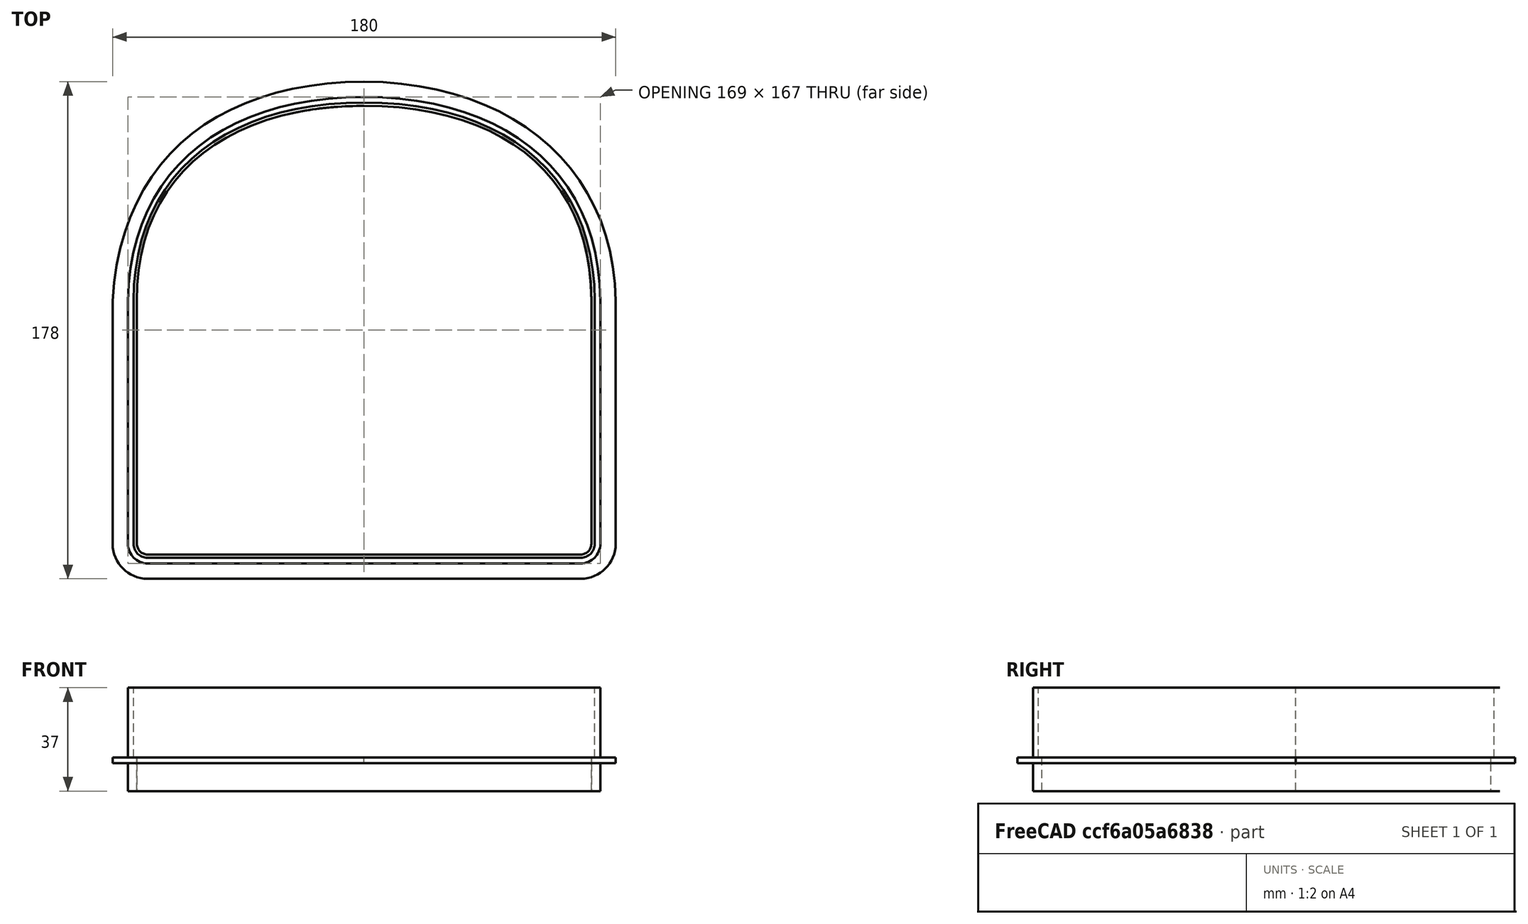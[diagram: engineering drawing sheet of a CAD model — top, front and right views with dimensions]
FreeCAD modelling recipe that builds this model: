
FCSTD DOCUMENT  (FreeCAD 0.20R29410 (Git))
Label: CatDoorTunnel
License: All rights reserved
LicenseURL: http://en.wikipedia.org/wiki/All_rights_reserved
objects: Sketcher::SketchObject×6, PartDesign::Pad×5, PartDesign::Chamfer×2, PartDesign::Body×1
note: 21 computed .brp shape members not serialized (recipe doc carries the construction recipe); baked Part::Feature solids carry a one-line shape summary decoded from their .brp

FEATURE [Sketcher::SketchObject] Sketch
  FullyConstrained = true
  MapMode = 5
  Support = -> [XY_Plane]
  sketch-geometry (78):
    g0: LineSegment StartX=-82.5 StartY=-87 StartZ=0 EndX=-82.5 EndY=-2.2737e-12 EndZ=0
    g1: LineSegment StartX=82.5 StartY=-1.3709e-12 StartZ=0 EndX=82.5 EndY=-87 EndZ=0
    g2: LineSegment StartX=77.5 StartY=-92 StartZ=0 EndX=-77.5 EndY=-92 EndZ=0
    g3: ArcOfCircle CenterX=-77.5 CenterY=-87 CenterZ=0 NormalX=0 NormalY=0 NormalZ=1 AngleXU=0 Radius=5 StartAngle=3.14159 EndAngle=4.71239
    g4: ArcOfCircle CenterX=77.5 CenterY=-87 CenterZ=0 NormalX=0 NormalY=0 NormalZ=1 AngleXU=0 Radius=5 StartAngle=4.71239 EndAngle=6.28319
    g5: LineSegment StartX=-82.5 StartY=45 StartZ=0 EndX=-50 EndY=45 EndZ=0
    g6: LineSegment StartX=-50 StartY=45 StartZ=0 EndX=50 EndY=45 EndZ=0
    g7: LineSegment StartX=50 StartY=45 StartZ=0 EndX=82.5 EndY=45 EndZ=0
    g8: LineSegment StartX=-50 StartY=71 StartZ=0 EndX=-50 EndY=45 EndZ=0
    g9: LineSegment StartX=50 StartY=71 StartZ=0 EndX=50 EndY=45 EndZ=0
    g10: LineSegment StartX=-82.5 StartY=71 StartZ=0 EndX=-50 EndY=71 EndZ=0
    g11: LineSegment StartX=50 StartY=71 StartZ=0 EndX=82.5 EndY=71 EndZ=0
    g12: LineSegment StartX=-82.5 StartY=45 StartZ=0 EndX=-82.5 EndY=71 EndZ=0
    g13: LineSegment StartX=82.5 StartY=71 StartZ=0 EndX=82.5 EndY=45 EndZ=0
    g14: LineSegment StartX=-50 StartY=71 StartZ=0 EndX=-8.37969 EndY=71 EndZ=0
    g15: LineSegment StartX=-8.37969 StartY=71 StartZ=0 EndX=-5.347e-13 EndY=71 EndZ=0
    g16: LineSegment StartX=-5.344e-13 StartY=71 StartZ=0 EndX=8.37969 EndY=71 EndZ=0
    g17: LineSegment StartX=8.37969 StartY=71 StartZ=0 EndX=50 EndY=71 EndZ=0
    g18: LineSegment StartX=-82.5 StartY=-2.2737e-12 StartZ=0 EndX=-82.5 EndY=3.37969 EndZ=0
    g19: LineSegment StartX=-82.5 StartY=3.37969 StartZ=0 EndX=-82.5 EndY=45 EndZ=0
    g20: LineSegment StartX=82.5 StartY=45 StartZ=0 EndX=82.5 EndY=3.37969 EndZ=0
    g21: LineSegment StartX=82.5 StartY=3.37969 StartZ=0 EndX=82.5 EndY=-1.3709e-12 EndZ=0
    g22: LineSegment StartX=-82.5 StartY=3.37969 StartZ=0 EndX=82.5 EndY=3.37969 EndZ=0
    g23: LineSegment StartX=-8.37969 StartY=71 StartZ=0 EndX=-8.37969 EndY=-92 EndZ=0
    g24: LineSegment StartX=50 StartY=71 StartZ=0 EndX=82.5 EndY=45 EndZ=0
    g25: LineSegment StartX=-82.5 StartY=45 StartZ=0 EndX=-50 EndY=71 EndZ=0
    g26: LineSegment StartX=-5.344e-13 StartY=73 StartZ=0 EndX=-5.344e-13 EndY=71 EndZ=0
    g27: LineSegment StartX=-5.344e-13 StartY=71 StartZ=0 EndX=-5.344e-13 EndY=69.8 EndZ=0
    g28: LineSegment StartX=50.662 StartY=72.8873 StartZ=0 EndX=50 EndY=71 EndZ=0
    g29: LineSegment StartX=50 StartY=71 StartZ=0 EndX=49.6028 EndY=69.8676 EndZ=0
    g30: LineSegment StartX=49.6028 StartY=69.8676 StartZ=0 EndX=45.4398 EndY=58 EndZ=0
    g31: LineSegment StartX=84.3026 StartY=45.8664 StartZ=0 EndX=82.5 EndY=45 EndZ=0
    g32: LineSegment StartX=82.5 StartY=45 StartZ=0 EndX=81.4184 EndY=44.4802 EndZ=0
    g33: LineSegment StartX=81.4184 StartY=44.4802 StartZ=0 EndX=66.25 EndY=37.1898 EndZ=0
    g34: LineSegment StartX=-50.662 StartY=72.8873 StartZ=0 EndX=-50 EndY=71 EndZ=0
    g35: LineSegment StartX=-50 StartY=71 StartZ=0 EndX=-49.6028 EndY=69.8676 EndZ=0
    g36: LineSegment StartX=-49.6028 StartY=69.8676 StartZ=0 EndX=-45.4398 EndY=58 EndZ=0
    g37: LineSegment StartX=-83.7309 StartY=46.5763 StartZ=0 EndX=-82.5 EndY=45 EndZ=0
    g38: LineSegment StartX=-82.5 StartY=45 StartZ=0 EndX=-81.7615 EndY=44.0542 EndZ=0
    g39: LineSegment StartX=-81.7615 StartY=44.0542 StartZ=0 EndX=-66.25 EndY=24.1898 EndZ=0
    g40: LineSegment StartX=-82.5 StartY=-2.2737e-12 StartZ=0 EndX=-84.5 EndY=-2.2737e-12 EndZ=0
    g41: LineSegment StartX=-82.5 StartY=-2.2737e-12 StartZ=0 EndX=-81.3 EndY=-2.2737e-12 EndZ=0
    g42: LineSegment StartX=-82.5 StartY=-87 StartZ=0 EndX=-84.5 EndY=-87 EndZ=0
    g43: LineSegment StartX=-82.5 StartY=-87 StartZ=0 EndX=-81.3 EndY=-87 EndZ=0
    g44: LineSegment StartX=-77.5 StartY=-92 StartZ=0 EndX=-77.5 EndY=-94 EndZ=0
    g45: LineSegment StartX=-77.5 StartY=-92 StartZ=0 EndX=-77.5 EndY=-90.8 EndZ=0
    g46: LineSegment StartX=77.5 StartY=-92 StartZ=0 EndX=77.5 EndY=-94 EndZ=0
    g47: LineSegment StartX=77.5 StartY=-92 StartZ=0 EndX=77.5 EndY=-90.8 EndZ=0
    g48: LineSegment StartX=82.5 StartY=-87 StartZ=0 EndX=81.3 EndY=-87 EndZ=0
    g49: LineSegment StartX=82.5 StartY=-87 StartZ=0 EndX=84.5 EndY=-87 EndZ=0
    g50: LineSegment StartX=82.5 StartY=-1.3709e-12 StartZ=0 EndX=84.5 EndY=-1.3709e-12 EndZ=0
    g51: LineSegment StartX=82.5 StartY=-1.3709e-12 StartZ=0 EndX=81.3 EndY=-1.3709e-12 EndZ=0
    g52: ArcOfCircle CenterX=-77.5 CenterY=-87 CenterZ=0 NormalX=0 NormalY=0 NormalZ=1 AngleXU=0 Radius=7 StartAngle=3.14159 EndAngle=4.71239
    g53: ArcOfCircle CenterX=-77.5 CenterY=-87 CenterZ=0 NormalX=0 NormalY=0 NormalZ=1 AngleXU=0 Radius=3.8 StartAngle=3.14159 EndAngle=4.71239
    g54: ArcOfCircle CenterX=77.5 CenterY=-87 CenterZ=0 NormalX=0 NormalY=0 NormalZ=1 AngleXU=0 Radius=3.8 StartAngle=4.71239 EndAngle=6.28319
    g55: ArcOfCircle CenterX=77.5 CenterY=-87 CenterZ=0 NormalX=0 NormalY=0 NormalZ=1 AngleXU=0 Radius=7 StartAngle=4.71239 EndAngle=6.28319
    g56: LineSegment StartX=-77.5 StartY=-94 StartZ=0 EndX=77.5 EndY=-94 EndZ=0
    g57: LineSegment StartX=-77.5 StartY=-90.8 StartZ=0 EndX=77.5 EndY=-90.8 EndZ=0
    g58: LineSegment StartX=84.5 StartY=-87 StartZ=0 EndX=84.5 EndY=-1.3642e-12 EndZ=0
    g59: LineSegment StartX=81.3 StartY=-1.3709e-12 StartZ=0 EndX=81.3 EndY=-87 EndZ=0
    g60: LineSegment StartX=-81.3 StartY=-87 StartZ=0 EndX=-81.3 EndY=-2.2737e-12 EndZ=0
    g61: LineSegment StartX=-84.5 StartY=-87 StartZ=0 EndX=-84.5 EndY=-2.2737e-12 EndZ=0
    g62: LineSegment StartX=84.5 StartY=-1.3709e-12 StartZ=0 EndX=90 EndY=-1.3709e-12 EndZ=0
    g63: LineSegment StartX=84.5 StartY=-87 StartZ=0 EndX=90 EndY=-87 EndZ=0
    g64: LineSegment StartX=77.5 StartY=-94 StartZ=0 EndX=77.5 EndY=-99.5 EndZ=0
    g65: LineSegment StartX=-77.5 StartY=-94 StartZ=0 EndX=-77.5 EndY=-99.5 EndZ=0
    g66: LineSegment StartX=-84.5 StartY=-87 StartZ=0 EndX=-90 EndY=-87 EndZ=0
    g67: LineSegment StartX=-84.5 StartY=-2.2737e-12 StartZ=0 EndX=-90 EndY=-2.2737e-12 EndZ=0
    g68: LineSegment StartX=-83.7309 StartY=46.5763 StartZ=0 EndX=-87.1159 EndY=50.9113 EndZ=0
    g69: LineSegment StartX=-50.662 StartY=72.8873 StartZ=0 EndX=-52.4826 EndY=78.0772 EndZ=0
    g70: LineSegment StartX=-5.344e-13 StartY=73 StartZ=0 EndX=-5.344e-13 EndY=78.5 EndZ=0
    g71: LineSegment StartX=50.662 StartY=72.8873 StartZ=0 EndX=52.4826 EndY=78.0772 EndZ=0
    g72: LineSegment StartX=84.3026 StartY=45.8664 StartZ=0 EndX=89.2598 EndY=48.2489 EndZ=0
    g73: LineSegment StartX=-77.5 StartY=-99.5 StartZ=0 EndX=77.5 EndY=-99.5 EndZ=0
    g74: LineSegment StartX=-90 StartY=-2.2737e-12 StartZ=0 EndX=-90 EndY=-87 EndZ=0
    g75: LineSegment StartX=90 StartY=-87 StartZ=0 EndX=90 EndY=-1.3642e-12 EndZ=0
    g76: ArcOfCircle CenterX=-77.5 CenterY=-87 CenterZ=0 NormalX=0 NormalY=0 NormalZ=1 AngleXU=0 Radius=12.5 StartAngle=3.14159 EndAngle=4.71239
    g77: ArcOfCircle CenterX=77.5 CenterY=-87 CenterZ=0 NormalX=0 NormalY=0 NormalZ=1 AngleXU=0 Radius=12.5 StartAngle=4.71239 EndAngle=6.28319
  constraints (212):
    c: Coincident(g11,g13)
    c: Coincident(g12,g10)
    c: Coincident(g0,g18)
    c: Vertical(g0)
    c: Coincident(g21,g1)
    c: Horizontal(g2)
    c: Tangent(g0,g3) = 1.5708
    c: Tangent(g2,g3) = 1.5708
    c: Tangent(g1,g4) = 1.5708
    c: Vertical(g1)
    c: DistanceY(g2,g10) = 163
    c: DistanceY(g2,g0) = 92
    c: Radius(g3) = 5
    c: Horizontal(g5)
    c: Coincident(g6,g5)
    c: Horizontal(g6)
    c: Coincident(g7,g6)
    c: Horizontal(g7)
    c: Coincident(g8,g5)
    c: Vertical(g8)
    c: Vertical(g9)
    c: Coincident(g6,g9)
    c: Equal(g7,g5)
    c: DistanceY(g0,g5) = 45
    c: Coincident(g10,g14)
    c: Horizontal(g10)
    c: Coincident(g17,g11)
    c: Horizontal(g11)
    c: Coincident(g9,g17)
    c: Coincident(g8,g10)
    c: Coincident(g19,g12)
    c: Vertical(g12)
    c: Coincident(g13,g20)
    c: Vertical(g13)
    c: Coincident(g7,g13)
    c: Coincident(g5,g19)
    c: Coincident(g15,g16)
    c: Coincident(g14,g15)
    c: Horizontal(g14)
    c: Horizontal(g15)
    c: Coincident(g16,g17)
    c: Horizontal(g16)
    c: Equal(g15,g16)
    c: Equal(g14,g17)
    c: Tangent(g2,g4) = 1.5708
    c: Equal(g3,g4)
    c: Coincident(g18,g19)
    c: Vertical(g18)
    c: Vertical(g19)
    c: Coincident(g20,g21)
    c: Vertical(g20)
    c: Vertical(g21)
    c: Equal(g18,g21)
    c: Coincident(g22,g18)
    c: Coincident(g22,g20)
    c: Horizontal(g22)
    c: Coincident(g23,g14)
    c: PointOnObject(g23,g2)
    c: Vertical(g23)
    c: Coincident(g24,g9)
    c: Coincident(g24,g7)
    c: Coincident(g25,g5)
    c: Coincident(g25,g8)
    c: Equal(g17,g24)
    c: Equal(g24,g20)
    c: Equal(g19,g25)
    c: DistanceX(g8,g15) = 50
    c: Coincident(g26,g15)
    c: Vertical(g26)
    c: Coincident(g26,g27)
    c: Vertical(g27)
    c: Coincident(g28,g9)
    c: Coincident(g28,g29)
    c: Coincident(g29,g30)
    c: Parallel(g30,g29)
    c: Parallel(g29,g28)
    c: Symmetric(g7,g16,g30)
    c: Coincident(g31,g7)
    c: Coincident(g31,g32)
    c: Coincident(g32,g33)
    c: Parallel(g33,g32)
    c: Parallel(g32,g31)
    c: Symmetric(g28,g20,g33)
    c: Coincident(g34,g8)
    c: Coincident(g34,g35)
    c: Coincident(g35,g36)
    c: Coincident(g37,g5)
    c: Coincident(g37,g38)
    c: Coincident(g38,g39)
    c: Parallel(g36,g35)
    c: Parallel(g35,g34)
    c: Parallel(g37,g38)
    c: Parallel(g38,g39)
    c: Symmetric(g18,g5,g39)
    c: Symmetric(g37,g14,g36)
    c: Coincident(g40,g0)
    c: Horizontal(g40)
    c: Coincident(g41,g0)
    c: Horizontal(g41)
    c: Coincident(g42,g0)
    c: Coincident(g43,g0)
    c: Horizontal(g43)
    c: Coincident(g44,g2)
    c: Vertical(g44)
    c: Coincident(g45,g2)
    c: Vertical(g45)
    c: Coincident(g46,g2)
    c: Vertical(g46)
    c: Coincident(g47,g2)
    c: Vertical(g47)
    c: Coincident(g48,g1)
    c: Horizontal(g48)
    c: Coincident(g49,g1)
    c: Horizontal(g49)
    c: Coincident(g50,g1)
    c: Horizontal(g50)
    c: Coincident(g51,g1)
    c: Horizontal(g51)
    c: Equal(g42,g40)
    c: Equal(g40,g37)
    c: Equal(g37,g34)
    c: Equal(g34,g26)
    c: Equal(g26,g28)
    c: Equal(g28,g31)
    c: Equal(g31,g50)
    c: Equal(g50,g49)
    c: Equal(g49,g46)
    c: Equal(g46,g44)
    c: Equal(g43,g41)
    c: Equal(g41,g38)
    c: Equal(g38,g35)
    c: Equal(g35,g27)
    c: Equal(g27,g29)
    c: Equal(g29,g32)
    c: Equal(g32,g51)
    c: Equal(g51,g48)
    c: Equal(g48,g47)
    c: Equal(g47,g45)
    c: Horizontal(g42)
    c: DistanceX(g42,g0) = 2
    c: DistanceX(g43,g43) = 1.2
    c: Symmetric(g0,g1,g-1)  '__###__'
    c: Coincident(g52,g3)
    c: Coincident(g52,g42)
    c: PointOnObject(g52,g44)
    c: Coincident(g53,g3)
    c: Coincident(g53,g43)
    c: PointOnObject(g53,g45)
    c: Coincident(g54,g4)
    c: Coincident(g54,g48)
    c: PointOnObject(g54,g47)
    c: Coincident(g55,g4)
    c: Coincident(g55,g49)
    c: PointOnObject(g55,g46)
    c: Coincident(g56,g52)
    c: Coincident(g56,g55)
    c: Coincident(g57,g53)
    c: Coincident(g57,g54)
    c: Coincident(g58,g55)
    c: Coincident(g58,g50)
    c: Coincident(g59,g51)
    c: Coincident(g59,g54)
    c: Coincident(g60,g53)
    c: Coincident(g60,g41)
    c: Coincident(g61,g52)
    c: Coincident(g61,g40)
    c: DistanceX(g0,g1) = 165
    c: Coincident(g62,g50)
    c: Horizontal(g62)
    c: Coincident(g63,g49)
    c: Horizontal(g63)
    c: Coincident(g64,g46)
    c: Vertical(g64)
    c: Coincident(g65,g44)
    c: Vertical(g65)
    c: Coincident(g66,g42)
    c: Horizontal(g66)
    c: Coincident(g67,g40)
    c: Horizontal(g67)
    c: Coincident(g68,g37)
    c: Coincident(g69,g34)
    c: Coincident(g70,g26)
    c: Vertical(g70)
    c: Coincident(g71,g28)
    c: Coincident(g72,g31)
    c: Parallel(g72,g31)
    c: Parallel(g71,g28)
    c: Parallel(g69,g34)
    c: Parallel(g68,g37)
    c: Equal(g66,g65)
    c: Equal(g65,g64)
    c: Equal(g72,g71)
    c: Equal(g71,g70)
    c: Equal(g70,g69)
    c: Equal(g69,g68)
    c: Coincident(g73,g65)
    c: Coincident(g73,g64)
    c: Equal(g64,g62)
    c: Equal(g68,g67)
    c: Coincident(g74,g67)
    c: Coincident(g74,g66)
    c: Vertical(g74)
    c: Coincident(g75,g63)
    c: Coincident(g75,g62)
    c: Vertical(g75)
    c: Coincident(g76,g3)
    c: Coincident(g76,g66)
    c: PointOnObject(g76,g65)
    c: Coincident(g77,g4)
    c: Coincident(g77,g64)
    c: PointOnObject(g77,g63)
    c: DistanceX(g66,g63) = 180
FEATURE [Sketcher::SketchObject] Sketch001
  ExternalGeometry = -> [Sketch]
  FullyConstrained = true
  MapMode = 5
  Support = -> [XY_Plane]
  sketch-geometry (38):
    g0: ArcOfCircle CenterX=-77.5 CenterY=-87 CenterZ=0 NormalX=0 NormalY=0 NormalZ=1 AngleXU=0 Radius=3.8 StartAngle=3.14159 EndAngle=4.71239
    g1: ArcOfCircle CenterX=-77.5 CenterY=-87 CenterZ=0 NormalX=0 NormalY=0 NormalZ=1 AngleXU=0 Radius=7 StartAngle=3.14159 EndAngle=4.71239
    g2: ArcOfCircle CenterX=77.5 CenterY=-87 CenterZ=0 NormalX=0 NormalY=0 NormalZ=1 AngleXU=0 Radius=3.8 StartAngle=4.71239 EndAngle=6.28319
    g3: ArcOfCircle CenterX=77.5 CenterY=-87 CenterZ=0 NormalX=0 NormalY=0 NormalZ=1 AngleXU=0 Radius=7 StartAngle=4.71239 EndAngle=6.28319
    g4: LineSegment StartX=-84.5 StartY=-87 StartZ=0 EndX=-84.5 EndY=7.23048e-11 EndZ=0
    g5: LineSegment StartX=-81.3 StartY=-87 StartZ=0 EndX=-81.3 EndY=1.5504e-11 EndZ=0
    g6: LineSegment StartX=-77.5 StartY=-90.8 StartZ=0 EndX=77.5 EndY=-90.8 EndZ=0
    g7: LineSegment StartX=-77.5 StartY=-94 StartZ=0 EndX=77.5 EndY=-94 EndZ=0
    g8: LineSegment StartX=81.3 StartY=-87 StartZ=0 EndX=81.3 EndY=-1.35e-12 EndZ=0
    g9: LineSegment StartX=84.5 StartY=-87 StartZ=0 EndX=84.5 EndY=-1.76641e-11 EndZ=0
    g10-g13: Circle x4 (B-spline internal-alignment scaffolding for g14; pole/knot coordinates omitted)
    g14: BSplineCurve PolesCount=4 KnotsCount=2 Degree=3 IsPeriodic=0
    g15: GeomPoint X=-84.5 Y=7.23048e-11 Z=0
    g16: GeomPoint X=5.34188e-11 Y=73 Z=0
    g17-g20: Circle x4 (B-spline internal-alignment scaffolding for g21; pole/knot coordinates omitted)
    g21: BSplineCurve PolesCount=4 KnotsCount=2 Degree=3 IsPeriodic=0
    g22: GeomPoint X=84.5 Y=-1.76641e-11 Z=0
    g23: GeomPoint X=5.34188e-11 Y=73 Z=0
    g24-g27: Circle x4 (B-spline internal-alignment scaffolding for g28; pole/knot coordinates omitted)
    g28: BSplineCurve PolesCount=4 KnotsCount=2 Degree=3 IsPeriodic=0
    g29: GeomPoint X=81.3 Y=-1.35e-12 Z=0
    g30: GeomPoint X=-4.88175e-11 Y=69.8 Z=0
    g31-g34: Circle x4 (B-spline internal-alignment scaffolding for g35; pole/knot coordinates omitted)
    g35: BSplineCurve PolesCount=4 KnotsCount=2 Degree=3 IsPeriodic=0
    g36: GeomPoint X=-81.3 Y=1.5504e-11 Z=0
    g37: GeomPoint X=-4.88175e-11 Y=69.8 Z=0
  constraints (68):
    c: Coincident(g4,g1)
    c: Coincident(g5,g0)
    c: Coincident(g6,g0)
    c: Coincident(g6,g2)
    c: Coincident(g7,g1)
    c: Coincident(g7,g3)
    c: Coincident(g8,g2)
    c: Coincident(g9,g3)
    c: Weight(g10) = 1
    c: Coincident(g14,g4)
    c: Equal(g10,g11)
    c: Equal(g10,g12)
    c: Equal(g10,g13)
    c: InternalAlignment(g10-g13 -> g14) x4
    c: InternalAlignment(g15,g14)
    c: InternalAlignment(g16,g14)
    c: Weight(g17) = 1
    c: Coincident(g21,g9)
    c: Equal(g17,g18)
    c: Equal(g17,g19)
    c: Equal(g17,g20)
    c: Coincident(g21,g14)
    c: InternalAlignment(g17-g20 -> g21) x4
    c: InternalAlignment(g22,g21)
    c: InternalAlignment(g23,g21)
    c: Weight(g24) = 1
    c: Coincident(g28,g8)
    c: Equal(g24,g25)
    c: Equal(g24,g26)
    c: Equal(g24,g27)
    c: InternalAlignment(g24-g27 -> g28) x4
    c: InternalAlignment(g29,g28)
    c: InternalAlignment(g30,g28)
    c: Weight(g31) = 1
    c: Coincident(g35,g5)
    c: Equal(g31,g32)
    c: Equal(g31,g33)
    c: Equal(g31,g34)
    c: Coincident(g35,g28)
    c: InternalAlignment(g31-g34 -> g35) x4
    c: InternalAlignment(g36,g35)
    c: InternalAlignment(g37,g35)
    c: Equal(g3,g-6)
    c: Equal(g-5,g2)
    c: Equal(g-3,g1)
    c: Equal(g-4,g0)
    c: Coincident(g0,g-4)
    c: Coincident(g0,g-4)
    c: Coincident(g2,g-5)
    c: Coincident(g2,g-5)
    c: Coincident(g3,g-6)
    c: Coincident(g3,g-6)
    c: Coincident(g1,g-3)
    c: Coincident(g1,g-3)
    c: Coincident(g5,g-9)
    c: Coincident(g32,g-11)
    c: Coincident(g-14,g33)
    c: Coincident(g28,g-15)
    c: Coincident(g14,g-16)
    c: Coincident(g12,g-13)
    c: Coincident(g11,g-12)
    c: Coincident(g4,g-10)
    c: Coincident(g19,g-18)
    c: Coincident(g18,g-20)
    c: Coincident(g9,g-8)
    c: Coincident(g8,g-7)
    c: Coincident(g25,g-19)
    c: Coincident(g26,g-17)
FEATURE [PartDesign::Pad] Pad
  Direction = (0,0,1)
  Length = 10
  Length2 = 10
  Profile = -> Sketch001
  ReferenceAxis = -> Sketch001 [N_Axis]
  Type = 0
FEATURE [Sketcher::SketchObject] Sketch002
  AttachmentOffset = pos=(0,0,10) rot=(0,0,1;0rad)
  ExternalGeometry = -> [Sketch]
  FullyConstrained = true
  MapMode = 5
  Placement = pos=(0,0,10) rot=(0,0,1;0rad)
  Support = -> [XY_Plane]
  expr: .AttachmentOffset.Base.z = <<Sketch001>>.AttachmentOffset.Base.z + <<Pad>>.Length
  sketch-geometry (38):
    g0: ArcOfCircle CenterX=-77.5 CenterY=-87 CenterZ=0 NormalX=0 NormalY=0 NormalZ=1 AngleXU=0 Radius=3.8 StartAngle=3.14159 EndAngle=4.71239
    g1: ArcOfCircle CenterX=-77.5 CenterY=-87 CenterZ=0 NormalX=0 NormalY=0 NormalZ=1 AngleXU=0 Radius=12.5 StartAngle=3.14159 EndAngle=4.71239
    g2: ArcOfCircle CenterX=77.5 CenterY=-87 CenterZ=0 NormalX=0 NormalY=0 NormalZ=1 AngleXU=0 Radius=3.8 StartAngle=4.71239 EndAngle=6.28319
    g3: ArcOfCircle CenterX=77.5 CenterY=-87 CenterZ=0 NormalX=0 NormalY=0 NormalZ=1 AngleXU=0 Radius=12.5 StartAngle=4.71239 EndAngle=6.28319
    g4: LineSegment StartX=-90 StartY=-87 StartZ=0 EndX=-90 EndY=2.02647e-11 EndZ=0
    g5: LineSegment StartX=-81.3 StartY=-87 StartZ=0 EndX=-81.3 EndY=-7.56586e-11 EndZ=0
    g6: LineSegment StartX=81.3 StartY=-87 StartZ=0 EndX=81.3 EndY=-1.3642e-12 EndZ=0
    g7: LineSegment StartX=90 StartY=-87 StartZ=0 EndX=90 EndY=-1.3642e-12 EndZ=0
    g8: LineSegment StartX=-77.5 StartY=-99.5 StartZ=0 EndX=77.5 EndY=-99.5 EndZ=0
    g9: LineSegment StartX=-77.5 StartY=-90.8 StartZ=0 EndX=77.5 EndY=-90.8 EndZ=0
    g10-g13: Circle x4 (B-spline internal-alignment scaffolding for g14; pole/knot coordinates omitted)
    g14: BSplineCurve PolesCount=4 KnotsCount=2 Degree=3 IsPeriodic=0
    g15: GeomPoint X=-81.3 Y=-7.56586e-11 Z=0
    g16: GeomPoint X=-6.08494e-11 Y=69.8 Z=0
    g17-g20: Circle x4 (B-spline internal-alignment scaffolding for g21; pole/knot coordinates omitted)
    g21: BSplineCurve PolesCount=4 KnotsCount=2 Degree=3 IsPeriodic=0
    g22: GeomPoint X=81.3 Y=-1.3642e-12 Z=0
    g23: GeomPoint X=-6.08494e-11 Y=69.8 Z=0
    g24-g27: Circle x4 (B-spline internal-alignment scaffolding for g28; pole/knot coordinates omitted)
    g28: BSplineCurve PolesCount=4 KnotsCount=2 Degree=3 IsPeriodic=0
    g29: GeomPoint X=-90 Y=2.02647e-11 Z=0
    g30: GeomPoint X=-2.37895e-11 Y=78.5 Z=0
    g31-g34: Circle x4 (B-spline internal-alignment scaffolding for g35; pole/knot coordinates omitted)
    g35: BSplineCurve PolesCount=4 KnotsCount=2 Degree=3 IsPeriodic=0
    g36: GeomPoint X=90 Y=-1.3642e-12 Z=0
    g37: GeomPoint X=-2.37895e-11 Y=78.5 Z=0
  constraints (68):
    c: Coincident(g4,g1)
    c: Coincident(g5,g0)
    c: Coincident(g6,g2)
    c: Coincident(g7,g3)
    c: Coincident(g8,g1)
    c: Coincident(g8,g3)
    c: Coincident(g9,g0)
    c: Coincident(g9,g2)
    c: Weight(g10) = 1
    c: Coincident(g14,g5)
    c: Equal(g10,g11)
    c: Equal(g10,g12)
    c: Equal(g10,g13)
    c: InternalAlignment(g10-g13 -> g14) x4
    c: InternalAlignment(g15,g14)
    c: InternalAlignment(g16,g14)
    c: Weight(g17) = 1
    c: Coincident(g21,g6)
    c: Equal(g17,g18)
    c: Equal(g17,g19)
    c: Equal(g17,g20)
    c: Coincident(g21,g14)
    c: InternalAlignment(g17-g20 -> g21) x4
    c: InternalAlignment(g22,g21)
    c: InternalAlignment(g23,g21)
    c: Weight(g24) = 1
    c: Coincident(g28,g4)
    c: Equal(g24,g25)
    c: Equal(g24,g26)
    c: Equal(g24,g27)
    c: InternalAlignment(g24-g27 -> g28) x4
    c: InternalAlignment(g29,g28)
    c: InternalAlignment(g30,g28)
    c: Weight(g31) = 1
    c: Coincident(g35,g7)
    c: Equal(g31,g32)
    c: Equal(g31,g33)
    c: Equal(g31,g34)
    c: Coincident(g35,g28)
    c: InternalAlignment(g31-g34 -> g35) x4
    c: InternalAlignment(g36,g35)
    c: InternalAlignment(g37,g35)
    c: Equal(g1,g-4)
    c: Equal(g-3,g0)
    c: Equal(g-6,g3)
    c: Equal(g2,g-5)
    c: Coincident(g2,g-5)
    c: Coincident(g2,g-5)
    c: Coincident(g3,g-6)
    c: Coincident(g3,g-6)
    c: Coincident(g1,g-4)
    c: Coincident(g1,g-4)
    c: Coincident(g0,g-3)
    c: Coincident(g0,g-3)
    c: Coincident(g5,g-20)
    c: Coincident(g4,g-19)
    c: Coincident(g7,g-8)
    c: Coincident(g6,g-7)
    c: Coincident(g18,g-9)
    c: Coincident(g32,g-10)
    c: Coincident(g33,g-11)
    c: Coincident(g19,g-12)
    c: Coincident(g14,g-14)
    c: Coincident(g28,g-13)
    c: Coincident(g26,g-15)
    c: Coincident(g12,g-16)
    c: Coincident(g25,g-18)
    c: Coincident(g11,g-17)
FEATURE [PartDesign::Pad] Pad001
  BaseFeature = -> Pad
  Direction = (0,0,1)
  Length = 2
  Length2 = 10
  Profile = -> Sketch002
  ReferenceAxis = -> Sketch002 [N_Axis]
  Type = 0
FEATURE [Sketcher::SketchObject] Sketch003
  AttachmentOffset = pos=(0,0,12) rot=(0,0,1;0rad)
  ExternalGeometry = -> [Sketch]
  FullyConstrained = true
  MapMode = 5
  Placement = pos=(0,0,12) rot=(0,0,1;0rad)
  Support = -> [XY_Plane]
  expr: .AttachmentOffset.Base.z = <<Sketch002>>.AttachmentOffset.Base.z + <<Pad001>>.Length
  sketch-geometry (38):
    g0: ArcOfCircle CenterX=-77.5 CenterY=-87 CenterZ=0 NormalX=0 NormalY=0 NormalZ=1 AngleXU=0 Radius=5 StartAngle=3.14159 EndAngle=4.71239
    g1: ArcOfCircle CenterX=-77.5 CenterY=-87 CenterZ=0 NormalX=0 NormalY=0 NormalZ=1 AngleXU=0 Radius=7 StartAngle=3.14159 EndAngle=4.71239
    g2: ArcOfCircle CenterX=77.5 CenterY=-87 CenterZ=0 NormalX=0 NormalY=0 NormalZ=1 AngleXU=0 Radius=7 StartAngle=4.71239 EndAngle=6.28319
    g3: LineSegment StartX=-84.5 StartY=-87 StartZ=0 EndX=-84.5 EndY=5.87903e-11 EndZ=0
    g4: LineSegment StartX=-82.5 StartY=-87 StartZ=0 EndX=-82.5 EndY=1.705e-13 EndZ=0
    g5: LineSegment StartX=82.5 StartY=-87 StartZ=0 EndX=82.5 EndY=-4.31726e-11 EndZ=0
    g6: LineSegment StartX=84.5 StartY=-87 StartZ=0 EndX=84.5 EndY=5.03064e-11 EndZ=0
    g7: LineSegment StartX=77.5 StartY=-92 StartZ=0 EndX=-77.5 EndY=-92 EndZ=0
    g8: LineSegment StartX=77.5 StartY=-94 StartZ=0 EndX=-77.5 EndY=-94 EndZ=0
    g9-g12: Circle x4 (B-spline internal-alignment scaffolding for g13; pole/knot coordinates omitted)
    g13: BSplineCurve PolesCount=4 KnotsCount=2 Degree=3 IsPeriodic=0
    g14: GeomPoint X=-82.5 Y=1.705e-13 Z=0
    g15: GeomPoint X=-7.50191e-11 Y=71 Z=0
    g16-g19: Circle x4 (B-spline internal-alignment scaffolding for g20; pole/knot coordinates omitted)
    g20: BSplineCurve PolesCount=4 KnotsCount=2 Degree=3 IsPeriodic=0
    g21: GeomPoint X=82.5 Y=-4.31726e-11 Z=0
    g22: GeomPoint X=-7.50191e-11 Y=71 Z=0
    g23-g26: Circle x4 (B-spline internal-alignment scaffolding for g27; pole/knot coordinates omitted)
    g27: BSplineCurve PolesCount=4 KnotsCount=2 Degree=3 IsPeriodic=0
    g28: GeomPoint X=-84.5 Y=5.87903e-11 Z=0
    g29: GeomPoint X=2.95461e-11 Y=73 Z=0
    g30-g33: Circle x4 (B-spline internal-alignment scaffolding for g34; pole/knot coordinates omitted)
    g34: BSplineCurve PolesCount=4 KnotsCount=2 Degree=3 IsPeriodic=0
    g35: GeomPoint X=84.5 Y=5.03064e-11 Z=0
    g36: GeomPoint X=2.95461e-11 Y=73 Z=0
    g37: ArcOfCircle CenterX=77.5 CenterY=-87 CenterZ=0 NormalX=0 NormalY=0 NormalZ=1 AngleXU=0 Radius=5 StartAngle=4.71239 EndAngle=6.28319
  constraints (68):
    c: Coincident(g3,g1)
    c: Coincident(g4,g0)
    c: Coincident(g6,g2)
    c: Coincident(g7,g0)
    c: Coincident(g8,g2)
    c: Coincident(g8,g1)
    c: Weight(g9) = 1
    c: Coincident(g13,g4)
    c: Equal(g9,g10)
    c: Equal(g9,g11)
    c: Equal(g9,g12)
    c: InternalAlignment(g9-g12 -> g13) x4
    c: InternalAlignment(g14,g13)
    c: InternalAlignment(g15,g13)
    c: Weight(g16) = 1
    c: Coincident(g20,g5)
    c: Equal(g16,g17)
    c: Equal(g16,g18)
    c: Equal(g16,g19)
    c: InternalAlignment(g16-g19 -> g20) x4
    c: InternalAlignment(g21,g20)
    c: InternalAlignment(g22,g20)
    c: Coincident(g13,g20)
    c: Weight(g23) = 1
    c: Coincident(g27,g3)
    c: Equal(g23,g24)
    c: Equal(g23,g25)
    c: Equal(g23,g26)
    c: InternalAlignment(g23-g26 -> g27) x4
    c: InternalAlignment(g28,g27)
    c: InternalAlignment(g29,g27)
    c: Weight(g30) = 1
    c: Coincident(g34,g6)
    c: Equal(g30,g31)
    c: Equal(g30,g32)
    c: Equal(g30,g33)
    c: Coincident(g34,g27)
    c: InternalAlignment(g30-g33 -> g34) x4
    c: InternalAlignment(g35,g34)
    c: InternalAlignment(g36,g34)
    c: Equal(g-5,g1)
    c: Equal(g-6,g0)
    c: Coincident(g0,g-6)
    c: Coincident(g-6,g0)
    c: Coincident(g1,g-5)
    c: Coincident(g1,g-5)
    c: Coincident(g2,g-4)
    c: Coincident(g2,g-4)
    c: Coincident(g6,g-13)
    c: Coincident(g5,g-13)
    c: Coincident(g17,g-12)
    c: Coincident(g31,g-12)
    c: Coincident(g32,g-11)
    c: Coincident(g18,g-11)
    c: Coincident(g27,g-10)
    c: Coincident(g13,g-10)
    c: Coincident(g11,g-9)
    c: Coincident(g25,g-9)
    c: Coincident(g24,g-8)
    c: Coincident(g10,g-8)
    c: Coincident(g3,g-7)
    c: Coincident(g4,g-7)
    c: Equal(g-4,g2)
    c: Coincident(g7,g-3)
    c: Coincident(g5,g-3)
    c: Coincident(g37,g7)
    c: Coincident(g37,g5)
    c: Equal(g37,g-3)
FEATURE [PartDesign::Pad] Pad002
  BaseFeature = -> Pad001
  Direction = (0,0,1)
  Length = 25
  Length2 = 10
  Profile = -> Sketch003
  ReferenceAxis = -> Sketch003 [N_Axis]
  Type = 0
FEATURE [PartDesign::Chamfer] Chamfer
  Angle = 45
  Base = -> Pad002 [Edge74]
  BaseFeature = -> Pad002
  ChamferType = 0
  FlipDirection = false
  Size = 1
  Size2 = 1
  SupportTransform = false
  UseAllEdges = false
FEATURE [Sketcher::SketchObject] Sketch004
  AttachmentOffset = pos=(0,0,37) rot=(0,0,1;0rad)
  ExternalGeometry = -> [Sketch]
  FullyConstrained = true
  MapMode = 5
  Placement = pos=(0,0,37) rot=(0,0,1;0rad)
  Support = -> [XY_Plane]
  expr: .AttachmentOffset.Base.z = <<Sketch003>>.AttachmentOffset.Base.z + <<Pad002>>.Length
  sketch-geometry (37):
    g0: ArcOfCircle CenterX=-77.5 CenterY=-87 CenterZ=0 NormalX=0 NormalY=0 NormalZ=1 AngleXU=0 Radius=3.8 StartAngle=3.14159 EndAngle=4.71239
    g1: ArcOfCircle CenterX=-77.5 CenterY=-87 CenterZ=0 NormalX=0 NormalY=0 NormalZ=1 AngleXU=0 Radius=7 StartAngle=3.14159 EndAngle=4.71239
    g2: ArcOfCircle CenterX=77.5 CenterY=-87 CenterZ=0 NormalX=0 NormalY=0 NormalZ=1 AngleXU=0 Radius=3.8 StartAngle=4.71239 EndAngle=6.28319
    g3: ArcOfCircle CenterX=77.5 CenterY=-87 CenterZ=0 NormalX=0 NormalY=0 NormalZ=1 AngleXU=0 Radius=7 StartAngle=4.71239 EndAngle=6.28319
    g4: LineSegment StartX=-84.5 StartY=-87 StartZ=0 EndX=-84.5 EndY=-2.70575e-11 EndZ=0
    g5: LineSegment StartX=-81.3 StartY=-87 StartZ=0 EndX=-81.3 EndY=4.45368e-11 EndZ=0
    g6: LineSegment StartX=-77.5 StartY=-90.8 StartZ=0 EndX=77.5 EndY=-90.8 EndZ=0
    g7: LineSegment StartX=-77.5 StartY=-94 StartZ=0 EndX=77.5 EndY=-94 EndZ=0
    g8: LineSegment StartX=81.3 StartY=-87 StartZ=0 EndX=81.3 EndY=-5.0591e-12 EndZ=0
    g9: LineSegment StartX=84.5 StartY=-87 StartZ=0 EndX=84.5 EndY=2.6716e-12 EndZ=0
    g10-g13: Circle x4 (B-spline internal-alignment scaffolding for g14; pole/knot coordinates omitted)
    g14: BSplineCurve PolesCount=4 KnotsCount=2 Degree=3 IsPeriodic=0
    g15: GeomPoint X=-84.5 Y=-2.70575e-11 Z=0
    g16: GeomPoint X=4.61015e-11 Y=73 Z=0
    g17-g20: Circle x4 (B-spline internal-alignment scaffolding for g21; pole/knot coordinates omitted)
    g21: BSplineCurve PolesCount=4 KnotsCount=2 Degree=3 IsPeriodic=0
    g22: GeomPoint X=84.5 Y=2.6716e-12 Z=0
    g23: GeomPoint X=4.61015e-11 Y=73 Z=0
    g24-g27: Circle x4 (B-spline internal-alignment scaffolding for g28; pole/knot coordinates omitted)
    g28: BSplineCurve PolesCount=4 KnotsCount=2 Degree=3 IsPeriodic=0
    g29: GeomPoint X=81.3 Y=-5.0591e-12 Z=0
    g30: GeomPoint X=-4.09779e-11 Y=69.8 Z=0
    g31-g34: Circle x4 (B-spline internal-alignment scaffolding for g35; pole/knot coordinates omitted)
    g35: BSplineCurve PolesCount=4 KnotsCount=2 Degree=3 IsPeriodic=0
    g36: GeomPoint X=-81.3 Y=4.45368e-11 Z=0
  constraints (67):
    c: Coincident(g4,g1)
    c: Coincident(g5,g0)
    c: Coincident(g6,g0)
    c: Coincident(g6,g2)
    c: Coincident(g7,g1)
    c: Coincident(g7,g3)
    c: Coincident(g8,g2)
    c: Coincident(g9,g3)
    c: Weight(g10) = 1
    c: Coincident(g14,g4)
    c: Equal(g10,g11)
    c: Equal(g10,g12)
    c: Equal(g10,g13)
    c: InternalAlignment(g10-g13 -> g14) x4
    c: InternalAlignment(g15,g14)
    c: InternalAlignment(g16,g14)
    c: Weight(g17) = 1
    c: Coincident(g21,g9)
    c: Equal(g17,g18)
    c: Equal(g17,g19)
    c: Equal(g17,g20)
    c: Coincident(g21,g14)
    c: InternalAlignment(g17-g20 -> g21) x4
    c: InternalAlignment(g22,g21)
    c: InternalAlignment(g23,g21)
    c: Weight(g24) = 1
    c: Coincident(g28,g8)
    c: Equal(g24,g25)
    c: Equal(g24,g26)
    c: Equal(g24,g27)
    c: InternalAlignment(g24-g27 -> g28) x4
    c: InternalAlignment(g29,g28)
    c: InternalAlignment(g30,g28)
    c: Weight(g31) = 1
    c: Coincident(g35,g5)
    c: Equal(g31,g32)
    c: Equal(g31,g33)
    c: Equal(g31,g34)
    c: Coincident(g35,g28)
    c: InternalAlignment(g31-g34 -> g35) x4
    c: InternalAlignment(g36,g35)
    c: Equal(g-3,g2)
    c: Equal(g-4,g3)
    c: Coincident(g3,g-4)
    c: Coincident(g-3,g2)
    c: Coincident(g-3,g2)
    c: Coincident(g-4,g3)
    c: Coincident(g-6,g0)
    c: Equal(g-5,g1)
    c: Equal(g-6,g0)
    c: Coincident(g1,g-5)
    c: Coincident(g0,g-6)
    c: Coincident(g-5,g1)
    c: Coincident(g5,g-7)
    c: Coincident(g4,g-8)
    c: Coincident(g32,g-9)
    c: Coincident(g11,g-10)
    c: Coincident(g33,g-12)
    c: Coincident(g12,g-11)
    c: Coincident(g14,g-14)
    c: Coincident(g28,g-13)
    c: Coincident(g26,g-15)
    c: Coincident(g19,g-16)
    c: Coincident(g18,g-18)
    c: Coincident(g25,g-17)
    c: Coincident(g9,g-20)
    c: Coincident(g8,g-19)
FEATURE [PartDesign::Pad] Pad003
  BaseFeature = -> Chamfer
  Direction = (0,0,1)
  Length = 2
  Length2 = 10
  Profile = -> Sketch004
  ReferenceAxis = -> Sketch004 [N_Axis]
  Type = 0
FEATURE [PartDesign::Chamfer] Chamfer001
  Angle = 45
  Base = -> Pad003 [Edge95]
  BaseFeature = -> Pad003
  ChamferType = 0
  FlipDirection = false
  Size = 1.15
  Size2 = 1
  SupportTransform = false
  UseAllEdges = false
FEATURE [Sketcher::SketchObject] Sketch005
  AttachmentOffset = pos=(0,0,39) rot=(0,0,1;0rad)
  ExternalGeometry = -> [Sketch]
  FullyConstrained = true
  MapMode = 5
  Placement = pos=(0,0,39) rot=(0,0,1;0rad)
  Support = -> [XY_Plane]
  expr: .AttachmentOffset.Base.z = <<Sketch004>>.AttachmentOffset.Base.z + <<Pad003>>.Length
  sketch-geometry (38):
    g0: ArcOfCircle CenterX=77.5 CenterY=-87 CenterZ=0 NormalX=0 NormalY=0 NormalZ=1 AngleXU=0 Radius=3.8 StartAngle=4.71239 EndAngle=6.28319
    g1: ArcOfCircle CenterX=77.5 CenterY=-87 CenterZ=0 NormalX=0 NormalY=0 NormalZ=1 AngleXU=0 Radius=5 StartAngle=4.71239 EndAngle=6.28319
    g2: ArcOfCircle CenterX=-77.5 CenterY=-87 CenterZ=0 NormalX=0 NormalY=0 NormalZ=1 AngleXU=0 Radius=3.8 StartAngle=3.14159 EndAngle=4.71239
    g3: ArcOfCircle CenterX=-77.5 CenterY=-87 CenterZ=0 NormalX=0 NormalY=0 NormalZ=1 AngleXU=0 Radius=5 StartAngle=3.14159 EndAngle=4.71239
    g4: LineSegment StartX=-82.5 StartY=-87 StartZ=0 EndX=-82.5 EndY=-4.65121e-11 EndZ=0
    g5: LineSegment StartX=-81.3 StartY=-87 StartZ=0 EndX=-81.3 EndY=-2.2879e-12 EndZ=0
    g6: LineSegment StartX=-77.5 StartY=-90.8 StartZ=0 EndX=77.5 EndY=-90.8 EndZ=0
    g7: LineSegment StartX=-77.5 StartY=-92 StartZ=0 EndX=77.5 EndY=-92 EndZ=0
    g8: LineSegment StartX=81.3 StartY=-87 StartZ=0 EndX=81.3 EndY=-1.3785e-12 EndZ=0
    g9: LineSegment StartX=82.5 StartY=-87 StartZ=0 EndX=82.5 EndY=5.61471e-11 EndZ=0
    g10-g13: Circle x4 (B-spline internal-alignment scaffolding for g14; pole/knot coordinates omitted)
    g14: BSplineCurve PolesCount=4 KnotsCount=2 Degree=3 IsPeriodic=0
    g15: GeomPoint X=-81.3 Y=-2.2879e-12 Z=0
    g16: GeomPoint X=-5.3e-13 Y=69.8 Z=0
    g17-g20: Circle x4 (B-spline internal-alignment scaffolding for g21; pole/knot coordinates omitted)
    g21: BSplineCurve PolesCount=4 KnotsCount=2 Degree=3 IsPeriodic=0
    g22: GeomPoint X=81.3 Y=-1.3785e-12 Z=0
    g23: GeomPoint X=-5.3e-13 Y=69.8 Z=0
    g24-g27: Circle x4 (B-spline internal-alignment scaffolding for g28; pole/knot coordinates omitted)
    g28: BSplineCurve PolesCount=4 KnotsCount=2 Degree=3 IsPeriodic=0
    g29: GeomPoint X=82.5 Y=5.61438e-11 Z=0
    g30: GeomPoint X=-5.292e-13 Y=71 Z=0
    g31-g34: Circle x4 (B-spline internal-alignment scaffolding for g35; pole/knot coordinates omitted)
    g35: BSplineCurve PolesCount=4 KnotsCount=2 Degree=3 IsPeriodic=0
    g36: GeomPoint X=-82.5 Y=-4.65121e-11 Z=0
    g37: GeomPoint X=-5.292e-13 Y=71 Z=0
  constraints (68):
    c: Coincident(g4,g3)
    c: Coincident(g5,g2)
    c: Coincident(g6,g2)
    c: Coincident(g6,g0)
    c: Coincident(g7,g3)
    c: Coincident(g7,g1)
    c: Coincident(g8,g0)
    c: Coincident(g9,g1)
    c: Weight(g10) = 1
    c: Coincident(g14,g5)
    c: Equal(g10,g11)
    c: Equal(g10,g12)
    c: Equal(g10,g13)
    c: InternalAlignment(g10-g13 -> g14) x4
    c: InternalAlignment(g15,g14)
    c: InternalAlignment(g16,g14)
    c: Weight(g17) = 1
    c: Coincident(g21,g8)
    c: Equal(g17,g18)
    c: Equal(g17,g19)
    c: Equal(g17,g20)
    c: Coincident(g21,g14)
    c: InternalAlignment(g17-g20 -> g21) x4
    c: InternalAlignment(g22,g21)
    c: InternalAlignment(g23,g21)
    c: Weight(g24) = 1
    c: Coincident(g28,g9)
    c: Equal(g24,g25)
    c: Equal(g24,g26)
    c: Equal(g24,g27)
    c: InternalAlignment(g24-g27 -> g28) x4
    c: InternalAlignment(g29,g28)
    c: InternalAlignment(g30,g28)
    c: Weight(g31) = 1
    c: Coincident(g35,g4)
    c: Equal(g31,g32)
    c: Coincident(g32,g-12)
    c: Equal(g31,g33)
    c: Coincident(g33,g-11)
    c: Equal(g31,g34)
    c: Coincident(g35,g28)
    c: InternalAlignment(g31-g34 -> g35) x4
    c: InternalAlignment(g36,g35)
    c: InternalAlignment(g37,g35)
    c: Equal(g-3,g2)
    c: Equal(g-4,g3)
    c: Equal(g-5,g0)
    c: Equal(g-6,g1)
    c: Coincident(g1,g-6)
    c: Coincident(g-5,g0)
    c: Coincident(g0,g-5)
    c: Coincident(g-6,g1)
    c: Coincident(g-4,g3)
    c: Coincident(g-3,g2)
    c: Coincident(g2,g-3)
    c: Coincident(g-4,g3)
    c: Coincident(g4,g-13)
    c: Coincident(g5,g-13)
    c: Coincident(g-12,g11)
    c: Coincident(g12,g-11)
    c: Coincident(g28,g-10)
    c: Coincident(g14,g-10)
    c: Coincident(g19,g-9)
    c: Coincident(g26,g-9)
    c: Coincident(g25,g-8)
    c: Coincident(g18,g-8)
    c: Coincident(g9,g-7)
    c: Coincident(g8,g-7)
FEATURE [PartDesign::Pad] Pad004
  BaseFeature = -> Chamfer001
  Direction = (0,0,1)
  Length = 9
  Length2 = 10
  Profile = -> Sketch005
  ReferenceAxis = -> Sketch005 [N_Axis]
  Refine = true
  Type = 0
FEATURE [PartDesign::Body] Body
  Group = -> [Sketch,Sketch001,Pad,Sketch002,Pad001,Sketch003,Pad002,Chamfer,Sketch004,Pad003,Chamfer001,Sketch005,Pad004]
  Origin = -> Origin
  Tip = -> Pad002
